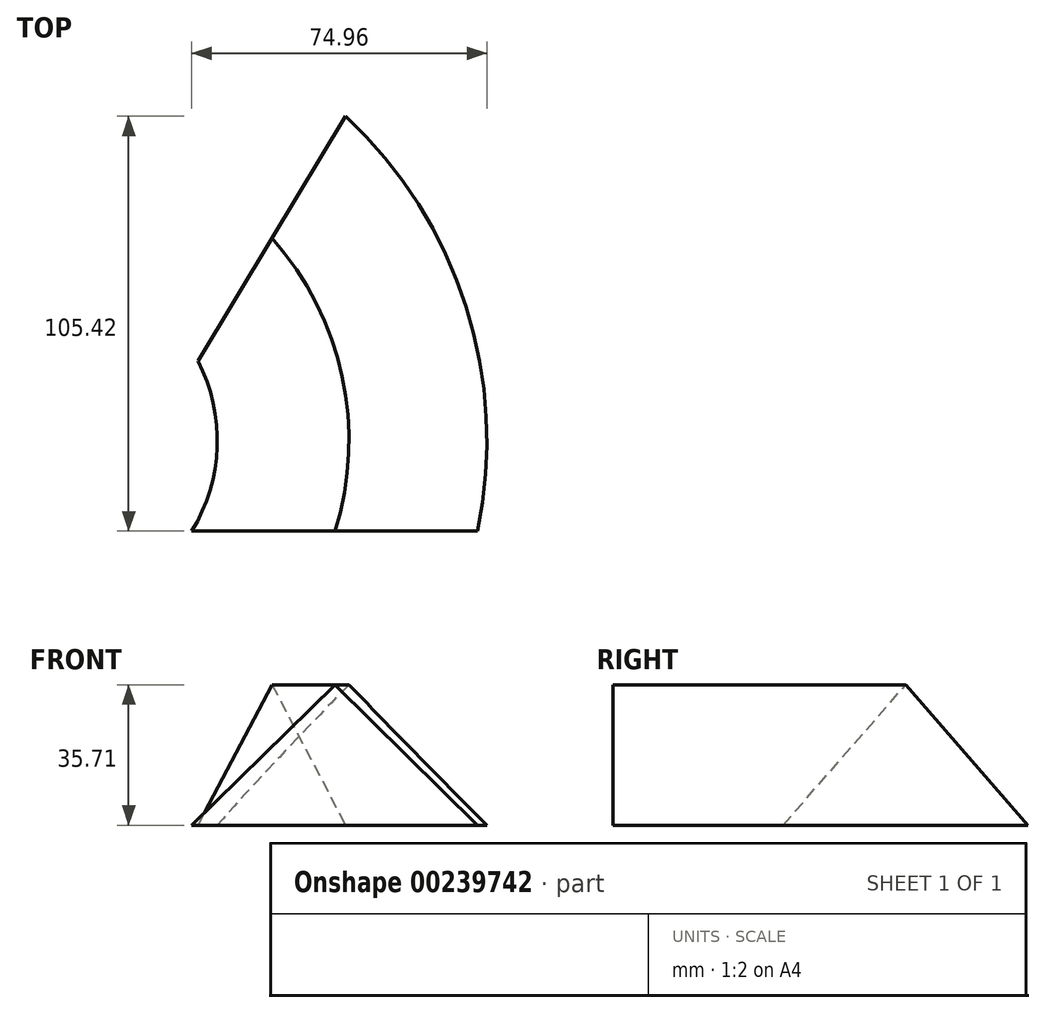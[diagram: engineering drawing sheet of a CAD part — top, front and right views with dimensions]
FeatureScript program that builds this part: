
annotation { "Feature Type Name" : "Feature", "Feature Type Description" : "" }
export const myFeature = defineFeature(function(context is Context, id is Id, definition is map)
    precondition{}
    {
        {
            var Q0;
            Q0=qCreatedBy(makeId("Front.planeOp"),FACE);
            var sketch = newSketch(context, id + "F0", { "sketchPlane" : qUnion([Q0])});
            skLineSegment(sketch, "E0", {"start": v(0, 35.7) * mm, "end": v(36.14, 0) * mm});
            skLineSegment(sketch, "E1", {"start": v(36.14, 0) * mm, "end": v(-36.43, 0) * mm});
            skLineSegment(sketch, "E2", {"start": v(-36.43, 0) * mm, "end": v(0, 35.7) * mm});
            skSolve(sketch);
        }
        {
            var Q0;
            Q0=qCreatedBy(makeId("Top.planeOp"),FACE);
            var sketch = newSketch(context, id + "F1", { "sketchPlane" : qUnion([Q0])});
            skArc(sketch, "E3", {"start": v(0, 0) * mm, "mid": v(1.77, 39.34) * mm, "end": v(-16.03, 74.47) * mm});
            skSolve(sketch);
        }
        {
            var Q0;
            Q0=makeQuery(id+"F0.imprint","IMPRINT",FACE,{"disambiguationData":[TD([[makeQuery(id+"F0.imprint","IMPRINT",EDGE,{"derivedFrom":sQuery(id+"F0.wireOp",EDGE,"E0")}),-1.0]])]});
            var Q1;
            Q1=sQuery(id+"F1.wireOp",EDGE,"E3");
            sweep(context, id + "F2", {"profiles" : qUnion([Q0]), "path" : qUnion([Q1])});
        }
    });
